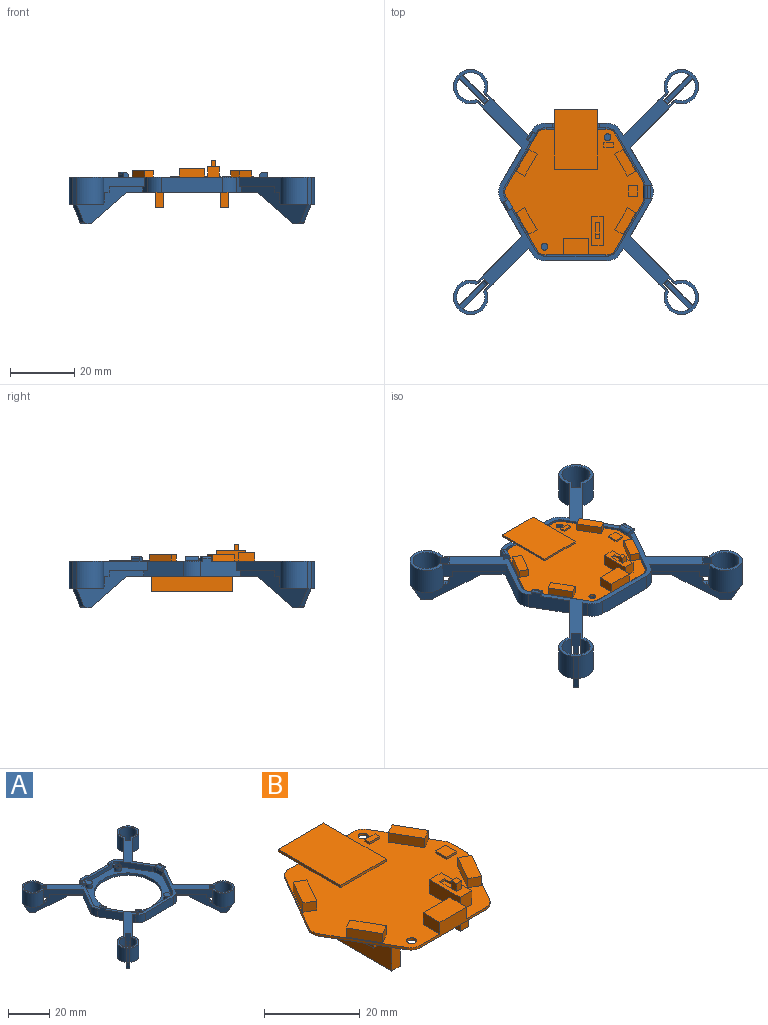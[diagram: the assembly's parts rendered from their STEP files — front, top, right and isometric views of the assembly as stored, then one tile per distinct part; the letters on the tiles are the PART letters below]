
ASSEMBLY  parts=2 mates=1
PART A: 187 faces, bbox 76.1x76.1x15.9 mm
  f0: plane 19.25x3.2mm, normal (0,1,0), area 60.2mm2, adj f2,f8,f69,f72,f78,f81,f117,f119
  f1: cylinder r=1.7mm len=3.4mm, axis (0,0,-1), area 22.2mm2, adj f72,f78,f118,f119
  f2: cylinder r=3.4mm len=3.2mm, axis (0,0,1), area 9.8mm2, adj f0,f8,f68,f72,f81,f116
  f3: plane 6.65x3.25mm, normal (0,0,1), area 10.1mm2, adj f4,f5,f62,f63,f71,f175,f184
  f4: plane 19.25x3.2mm, normal (0,-1,0), area 45.7mm2, adj f3,f7,f47,f63,f72,f75,f83,f113
  f5: plane 19.14x4.7mm, normal (0,1,0), area 75.5mm2, adj f3,f7,f23,f60,f71,f184,f185,f186
  f6: plane 41.4x23.95mm, normal (0,0,1), area 130.3mm2, adj f10,f11,f41,f45,f46,f49,f53,f61
  f7: plane 35.96x30.8mm, normal (0,0,1), area 137.2mm2, adj f4,f5,f13,f14,f39,f47,f58,f59
  f8: plane 76.11x35.96mm, normal (0,0,1), area 289.8mm2, adj f0,f2,f9,f15,f36,f37,f38,f41
  f9: cylinder r=5.35mm len=8.48mm, axis (0,0,1), area 119.1mm2, adj f8,f32,f52,f93,f100,f161
  f10: cylinder r=5.35mm len=8.48mm, axis (0,0,1), area 119.1mm2, adj f6,f28,f50,f88,f107,f160
  f11: cylinder r=5.35mm len=8.48mm, axis (0,0,1), area 119.1mm2, adj f6,f30,f33,f87,f106,f160
  f12: plane 4.18x0.46mm, normal (0,0,1), area 1.3mm2, adj f58,f162
  f13: cylinder r=5.35mm len=8.48mm, axis (0,0,1), area 119.1mm2, adj f7,f22,f85,f95,f110,f158
  f14: cylinder r=5.35mm len=8.48mm, axis (0,0,1), area 119.1mm2, adj f7,f24,f26,f84,f109,f158
  f15: cylinder r=5.35mm len=8.48mm, axis (0,0,1), area 119.1mm2, adj f8,f25,f90,f98,f103,f159
  f16: plane 20.55x20.55mm, normal (0.71,0.71,0), area 112.3mm2, adj f20,f23,f30,f33,f44,f45,f105,f120
  f17: plane 20.55x20.55mm, normal (0.71,-0.71,0), area 112.3mm2, adj f23,f25,f42,f54,f98,f102,f125,f145
  f18: plane 20.55x20.55mm, normal (-0.71,0.71,0), area 112.3mm2, adj f21,f22,f23,f39,f86,f95,f108,f126
  f19: plane 20.55x20.55mm, normal (-0.71,-0.71,0), area 112.3mm2, adj f23,f31,f34,f38,f73,f99,f131,f132
  f20: plane 5.38x3.4mm, normal (-0.61,0.61,-0.5), area 10.6mm2, adj f16,f121,f139,f160
  f21: plane 5.38x3.4mm, normal (0.61,0.61,-0.5), area 10.6mm2, adj f18,f128,f152,f158
  f22: plane 2.86x2.32mm, normal (0,0,-1), area 2.2mm2, adj f13,f18,f85,f108,f110,f126
  f23: plane 48.08x42.8mm, normal (0,0,-1), area 787.8mm2, adj f5,f16,f17,f18,f19,f37,f38,f39
  f24: plane 8.48x8.01mm, normal (0,0,-1), area 13mm2, adj f14,f94,f109,f128
  f25: plane 2.86x2.32mm, normal (0,0,-1), area 2.2mm2, adj f15,f17,f90,f102,f103,f125
  f26: plane 2.86x2.32mm, normal (0,0,-1), area 2.2mm2, adj f14,f84,f108,f109,f127,f128
  f27: plane 8.48x8.01mm, normal (0,0,-1), area 13mm2, adj f96,f97,f104,f124
  f28: plane 2.86x2.32mm, normal (0,0,-1), area 2.2mm2, adj f10,f88,f105,f107,f121,f122
  f29: plane 2.86x2.32mm, normal (0,0,-1), area 2.2mm2, adj f89,f96,f102,f104,f123,f124
  f30: plane 8.48x8.01mm, normal (0,0,-1), area 13mm2, adj f11,f16,f49,f106
  f31: plane 8.48x8.01mm, normal (0,0,-1), area 13mm2, adj f19,f36,f51,f101
  f32: plane 2.86x2.32mm, normal (0,0,-1), area 2.2mm2, adj f9,f93,f99,f100,f129,f130
  f33: plane 2.86x2.32mm, normal (0,0,-1), area 2.2mm2, adj f11,f16,f87,f105,f106,f120
  f34: plane 12.08x11.86mm, normal (0,0,-1), area 18.1mm2, adj f19,f38,f92,f131
  f35: plane 12.62x12.4mm, normal (0,0,-1), area 19mm2, adj f37,f93,f129,f130
  f36: cylinder r=5.35mm len=8.48mm, axis (0,0,1), area 119.1mm2, adj f8,f31,f73,f92,f101,f161
  f37: plane 12.47x7.2mm, normal (0.87,-0.5,0), area 64.2mm2, adj f8,f23,f35,f58,f93,f129
  f38: plane 4.7x2.41mm, normal (0.87,-0.5,0), area 9.6mm2, adj f8,f19,f23,f34,f57,f92
  f39: plane 4.7x2.41mm, normal (0.87,0.5,0), area 9.6mm2, adj f7,f18,f23,f60,f85,f86
  f40: plane 12.62x12.4mm, normal (0,0,-1), area 19mm2, adj f59,f84,f127,f128
  f41: plane 12.47x7.2mm, normal (-0.87,-0.5,0), area 67.2mm2, adj f6,f8,f23,f53,f89,f91,f124,f169
  f42: plane 12.08x11.86mm, normal (0,0,-1), area 18.1mm2, adj f17,f54,f90,f125
  f43: plane 12.62x12.4mm, normal (0,0,-1), area 19mm2, adj f46,f88,f121,f122
  f44: plane 12.08x11.86mm, normal (0,0,-1), area 18.1mm2, adj f16,f45,f87,f120
  f45: plane 5.7x2.6mm, normal (-0.87,0.5,0), area 12.6mm2, adj f6,f16,f23,f44,f71,f87,f173,f175
  f46: plane 12.47x7.2mm, normal (-0.87,0.5,0), area 64.2mm2, adj f6,f23,f43,f53,f88,f121
  f47: cylinder r=3.4mm len=3.2mm, axis (0,0,1), area 9.8mm2, adj f4,f7,f64,f72,f75,f112
  f48: cylinder r=1.7mm len=3.4mm, axis (0,0,-1), area 22.2mm2, adj f72,f75,f112,f113
  f49: cylinder r=4.35mm len=8.7mm, axis (0,0,1), area 205.6mm2, adj f6,f30,f50,f106,f107,f144
  f50: plane 8.48x8.01mm, normal (0,0,-1), area 13mm2, adj f10,f49,f107,f121
  f51: cylinder r=4.35mm len=8.7mm, axis (0,0,1), area 205.6mm2, adj f8,f31,f52,f100,f101,f132
  f52: plane 8.48x8.01mm, normal (0,0,-1), area 13mm2, adj f9,f51,f100,f129
  f53: cylinder r=5mm len=5mm, axis (0,0,1), area 24.6mm2, adj f6,f23,f41,f46
  f54: plane 4.7x2.41mm, normal (-0.87,-0.5,0), area 9.6mm2, adj f8,f17,f23,f42,f55,f90
  f55: cylinder r=5mm len=4.7mm, axis (0,0,1), area 24.6mm2, adj f8,f23,f54,f56
  f56: plane 19.14x4.7mm, normal (0,-1,0), area 90mm2, adj f8,f23,f55,f57
  f57: cylinder r=5mm len=4.7mm, axis (0,0,1), area 24.6mm2, adj f8,f23,f38,f56
  f58: cylinder r=5mm len=5mm, axis (0,0,1), area 24.6mm2, adj f7,f8,f12,f23,f37,f59
  f59: plane 12.47x7.2mm, normal (0.87,0.5,0), area 64.2mm2, adj f7,f23,f40,f58,f84,f128
  f60: cylinder r=5mm len=4.7mm, axis (0,0,1), area 24.6mm2, adj f5,f7,f23,f39
  f61: cylinder r=3.4mm len=3.4mm, axis (0,0,1), area 11.4mm2, adj f6,f62,f70,f72
  f62: plane 16.5x9.53mm, normal (0.87,-0.5,0), area 61mm2, adj f3,f6,f61,f63,f72,f177
  f63: cylinder r=3.4mm len=3.2mm, axis (0,0,1), area 9.8mm2, adj f3,f4,f62,f72,f83,f115
  f64: plane 14.41x8.32mm, normal (-0.87,-0.5,0), area 53.2mm2, adj f7,f47,f65,f72
  f65: cylinder r=3.4mm len=3.2mm, axis (0,0,1), area 5.7mm2, adj f7,f64,f66,f72
  f66: plane 4.18x3.2mm, normal (-1,0,0), area 13.4mm2, adj f65,f67,f72,f167
  f67: cylinder r=3.4mm len=3.2mm, axis (0,0,1), area 5.7mm2, adj f8,f66,f68,f72
  f68: plane 14.41x8.32mm, normal (-0.87,0.5,0), area 53.2mm2, adj f2,f8,f67,f72
  f69: cylinder r=3.4mm len=3.2mm, axis (0,0,1), area 9.8mm2, adj f0,f8,f70,f72,f78,f118
  f70: plane 16.5x9.53mm, normal (0.87,0.5,0), area 61mm2, adj f6,f8,f61,f69,f72,f172
  f71: cylinder r=5mm len=4.7mm, axis (0,0,1), area 24.6mm2, adj f3,f5,f23,f45
  f72: plane 43.9x39.8mm, normal (0,0,1), area 482.4mm2, adj f0,f1,f2,f4,f47,f48,f61,f62
  f73: plane 2.86x2.32mm, normal (0,0,-1), area 2.2mm2, adj f19,f36,f92,f99,f101,f131
  f74: cylinder r=1.05mm len=2.3mm, axis (0,0,-1), area 15.2mm2, adj f75,f76
  f75: plane 4.6x3.4mm, normal (0,0,1), area 6.8mm2, adj f4,f47,f48,f74,f112,f113
  f76: plane 2.1x2.1mm, normal (0,0,1), area 3.5mm2, adj f74
  f77: cylinder r=1.05mm len=2.3mm, axis (0,0,-1), area 15.2mm2, adj f78,f79
  f78: plane 4.6x3.4mm, normal (0,0,1), area 6.8mm2, adj f0,f1,f69,f77,f118,f119
  f79: plane 2.1x2.1mm, normal (0,0,1), area 3.5mm2, adj f77
  f80: cylinder r=1.7mm len=3.4mm, axis (0,0,-1), area 22.2mm2, adj f72,f81,f116,f117
  f81: plane 4.6x3.4mm, normal (0,0,1), area 10.3mm2, adj f0,f2,f80,f116,f117
  f82: cylinder r=1.7mm len=3.4mm, axis (0,0,-1), area 22.2mm2, adj f72,f83,f114,f115
  f83: plane 4.6x3.4mm, normal (0,0,1), area 10.3mm2, adj f4,f63,f82,f114,f115
  f84: plane 13.84x13.84mm, normal (0.71,-0.71,0), area 62mm2, adj f7,f14,f26,f40,f59,f127
  f85: plane 13.09x13.09mm, normal (-0.71,0.71,0), area 58.9mm2, adj f7,f13,f22,f39,f86,f126
  f86: plane 12.08x11.86mm, normal (0,0,-1), area 18.1mm2, adj f18,f39,f85,f126
  f87: plane 13.09x13.09mm, normal (0.71,0.71,0), area 58.9mm2, adj f6,f11,f33,f44,f45,f120
  f88: plane 13.84x13.84mm, normal (-0.71,-0.71,0), area 62mm2, adj f6,f10,f28,f43,f46,f122
  f89: plane 13.84x13.84mm, normal (-0.71,0.71,0), area 62mm2, adj f8,f29,f41,f91,f96,f123
  f90: plane 13.09x13.09mm, normal (0.71,-0.71,0), area 58.9mm2, adj f8,f15,f25,f42,f54,f125
  f91: plane 12.62x12.4mm, normal (0,0,-1), area 19mm2, adj f41,f89,f123,f124
  f92: plane 13.09x13.09mm, normal (-0.71,-0.71,0), area 58.9mm2, adj f8,f34,f36,f38,f73,f131
  f93: plane 13.84x13.84mm, normal (0.71,0.71,0), area 62mm2, adj f8,f9,f32,f35,f37,f130
  f94: cylinder r=4.35mm len=8.7mm, axis (0,0,1), area 205.6mm2, adj f7,f24,f95,f109,f110,f157
  f95: plane 8.48x8.01mm, normal (0,0,-1), area 13mm2, adj f13,f18,f94,f110
  f96: cylinder r=5.35mm len=8.48mm, axis (0,0,1), area 119.1mm2, adj f8,f27,f29,f89,f104,f159
  f97: cylinder r=4.35mm len=8.7mm, axis (0,0,1), area 205.6mm2, adj f8,f27,f98,f103,f104,f145
  f98: plane 8.48x8.01mm, normal (0,0,-1), area 13mm2, adj f15,f17,f97,f103
  f99: plane 7.4x1.98mm, normal (0.71,-0.71,0), area 17.8mm2, adj f8,f19,f32,f73,f100,f101,f129,f134
  f100: plane 8.4x1.93mm, normal (-0.71,-0.71,0), area 16.7mm2, adj f8,f9,f32,f51,f52,f99
  f101: plane 8.4x1.93mm, normal (0.71,0.71,0), area 16.7mm2, adj f8,f31,f36,f51,f73,f99
  f102: plane 7.4x1.98mm, normal (-0.71,-0.71,0), area 17.8mm2, adj f8,f17,f25,f29,f103,f104,f124,f146
  f103: plane 8.4x1.93mm, normal (-0.71,0.71,0), area 16.7mm2, adj f8,f15,f25,f97,f98,f102
  f104: plane 8.4x1.93mm, normal (0.71,-0.71,0), area 16.7mm2, adj f8,f27,f29,f96,f97,f102
  f105: plane 7.4x1.98mm, normal (-0.71,0.71,0), area 17.8mm2, adj f6,f16,f28,f33,f106,f107,f121,f143
  f106: plane 8.4x1.93mm, normal (-0.71,-0.71,0), area 16.7mm2, adj f6,f11,f30,f33,f49,f105
  f107: plane 8.4x1.93mm, normal (0.71,0.71,0), area 16.7mm2, adj f6,f10,f28,f49,f50,f105
  f108: plane 7.4x1.98mm, normal (0.71,0.71,0), area 17.8mm2, adj f7,f18,f22,f26,f109,f110,f128,f156
  f109: plane 8.4x1.93mm, normal (-0.71,0.71,0), area 16.7mm2, adj f7,f14,f24,f26,f94,f108
  f110: plane 8.4x1.93mm, normal (0.71,-0.71,0), area 16.7mm2, adj f7,f13,f22,f94,f95,f108
  f111: cylinder r=16.43mm len=32.86mm, axis (0,0,1), area 154.8mm2, adj f23,f72
  f112: plane 2.3x1.21mm, normal (1,0,0), area 2.8mm2, adj f47,f48,f72,f75
  f113: plane 2.3x1.28mm, normal (-1,0,0), area 2.9mm2, adj f4,f48,f72,f75
  f114: plane 2.3x1.28mm, normal (1,0,0), area 2.9mm2, adj f4,f72,f82,f83
  f115: plane 2.3x1.21mm, normal (-1,0,0), area 2.8mm2, adj f63,f72,f82,f83
  f116: plane 2.3x1.21mm, normal (1,0,0), area 2.8mm2, adj f2,f72,f80,f81
  f117: plane 2.3x1.28mm, normal (-1,0,0), area 2.9mm2, adj f0,f72,f80,f81
  f118: plane 2.3x1.21mm, normal (-1,0,0), area 2.8mm2, adj f1,f69,f72,f78
  f119: plane 2.3x1.28mm, normal (1,0,0), area 2.9mm2, adj f0,f1,f72,f78
  f120: plane 1.8x0.81mm, normal (0.71,-0.71,0), area 2.1mm2, adj f16,f33,f44,f87
  f121: plane 20.87x20.87mm, normal (-0.71,-0.71,0), area 113.1mm2, adj f20,f23,f28,f43,f46,f50,f105,f122
  f122: plane 1.8x0.81mm, normal (0.71,-0.71,0), area 2.1mm2, adj f28,f43,f88,f121
  f123: plane 1.8x0.81mm, normal (0.71,0.71,0), area 2.1mm2, adj f29,f89,f91,f124
  f124: plane 20.87x20.87mm, normal (-0.71,0.71,0), area 113.1mm2, adj f23,f27,f29,f41,f91,f102,f123,f145
  f125: plane 1.8x0.81mm, normal (0.71,0.71,0), area 2.1mm2, adj f17,f25,f42,f90
  f126: plane 1.8x0.81mm, normal (-0.71,-0.71,0), area 2.1mm2, adj f18,f22,f85,f86
  f127: plane 1.8x0.81mm, normal (-0.71,-0.71,0), area 2.1mm2, adj f26,f40,f84,f128
  f128: plane 20.87x20.87mm, normal (0.71,-0.71,0), area 113.1mm2, adj f21,f23,f24,f26,f40,f59,f108,f127
  f129: plane 20.87x20.87mm, normal (0.71,0.71,0), area 113.1mm2, adj f23,f32,f35,f37,f52,f99,f130,f132
  f130: plane 1.8x0.81mm, normal (-0.71,0.71,0), area 2.1mm2, adj f32,f35,f93,f129
  f131: plane 1.8x0.81mm, normal (-0.71,0.71,0), area 2.1mm2, adj f19,f34,f73,f92
  f132: plane 8.36x8.36mm, normal (0,0,1), area 17.3mm2, adj f19,f51,f129,f134
  f133: plane 5.38x3.4mm, normal (0.61,-0.61,-0.5), area 10.6mm2, adj f19,f129,f138,f161
  f134: cylinder r=1mm len=1.91mm, axis (0.71,0.71,0), area 2.7mm2, adj f19,f99,f129,f132
  f135: plane 12.16x12.16mm, normal (-0.37,0.37,-0.85), area 30.9mm2, adj f19,f23,f129,f136
  f136: cylinder r=1mm len=1.57mm, axis (0.71,0.71,0), area 0.9mm2, adj f19,f129,f135,f137
  f137: plane 2.71x2.71mm, normal (0,0,-1), area 3.6mm2, adj f19,f129,f136,f138
  f138: cylinder r=1mm len=1.81mm, axis (0.71,0.71,0), area 1.8mm2, adj f19,f129,f133,f137
  f139: cylinder r=1mm len=1.81mm, axis (0.71,0.71,0), area 1.8mm2, adj f16,f20,f121,f140
  f140: plane 2.71x2.71mm, normal (0,0,-1), area 3.6mm2, adj f16,f121,f139,f141
  f141: cylinder r=1mm len=1.57mm, axis (0.71,0.71,0), area 0.9mm2, adj f16,f121,f140,f142
  f142: plane 12.16x12.16mm, normal (0.37,-0.37,-0.85), area 30.9mm2, adj f16,f23,f121,f141
  f143: cylinder r=1mm len=1.91mm, axis (0.71,0.71,0), area 2.7mm2, adj f16,f105,f121,f144
  f144: plane 8.36x8.36mm, normal (0,0,1), area 17.3mm2, adj f16,f49,f121,f143
  f145: plane 8.36x8.36mm, normal (0,0,1), area 17.3mm2, adj f17,f97,f124,f146
  f146: cylinder r=1mm len=1.91mm, axis (0.71,-0.71,0), area 2.7mm2, adj f17,f102,f124,f145
  f147: plane 12.16x12.16mm, normal (0.37,0.37,-0.85), area 30.9mm2, adj f17,f23,f124,f148
  f148: cylinder r=1mm len=1.57mm, axis (0.71,-0.71,0), area 0.9mm2, adj f17,f124,f147,f149
  f149: plane 2.71x2.71mm, normal (0,0,-1), area 3.6mm2, adj f17,f124,f148,f150
  f150: cylinder r=1mm len=1.81mm, axis (0.71,-0.71,0), area 1.8mm2, adj f17,f124,f149,f151
  f151: plane 5.38x3.4mm, normal (-0.61,-0.61,-0.5), area 10.6mm2, adj f17,f124,f150,f159
  f152: cylinder r=1mm len=1.81mm, axis (0.71,-0.71,0), area 1.8mm2, adj f18,f21,f128,f153
  f153: plane 2.71x2.71mm, normal (0,0,-1), area 3.6mm2, adj f18,f128,f152,f154
  f154: cylinder r=1mm len=1.57mm, axis (0.71,-0.71,0), area 0.9mm2, adj f18,f128,f153,f155
  f155: plane 12.16x12.16mm, normal (-0.37,-0.37,-0.85), area 30.9mm2, adj f18,f23,f128,f154
  f156: cylinder r=1mm len=1.91mm, axis (0.71,-0.71,0), area 2.7mm2, adj f18,f108,f128,f157
  f157: plane 8.36x8.36mm, normal (0,0,1), area 17.3mm2, adj f18,f94,f128,f156
  f158: plane 8.52x1.2mm, normal (0.71,0.71,0), area 14.5mm2, adj f7,f13,f14,f18,f21,f128
  f159: plane 8.52x1.2mm, normal (-0.71,-0.71,0), area 14.5mm2, adj f8,f15,f17,f96,f124,f151
  f160: plane 8.52x1.2mm, normal (-0.71,0.71,0), area 14.5mm2, adj f6,f10,f11,f16,f20,f121
  f161: plane 8.52x1.2mm, normal (0.71,-0.71,0), area 14.5mm2, adj f8,f9,f19,f36,f129,f133
  f162: plane 4.18x1mm, normal (1,0,0), area 4.2mm2, adj f12,f163,f165,f180
  f163: plane 2.73x1.5mm, normal (0,1,0), area 3.7mm2, adj f7,f162,f164,f166,f167,f180,f183
  f164: plane 4.18x0.2mm, normal (-1,0,0), area 0.8mm2, adj f163,f165,f167,f183
  f165: plane 2.73x1.5mm, normal (0,-1,0), area 3.7mm2, adj f8,f162,f164,f166,f167,f180,f183
  f166: plane 4.18x0.93mm, normal (0,0,1), area 3.9mm2, adj f163,f165,f180,f183
  f167: plane 4.18x0.5mm, normal (0,0,-1), area 2.1mm2, adj f66,f163,f164,f165
  f168: plane 2.6x1.5mm, normal (0.87,0.5,0), area 0.6mm2, adj f169,f170,f172,f182
  f169: plane 1.73x1.5mm, normal (-0.5,0.87,0), area 2.6mm2, adj f6,f41,f168,f171,f172,f179,f182
  f170: plane 1.73x1.5mm, normal (0.5,-0.87,0), area 2.6mm2, adj f8,f41,f168,f171,f172,f179,f182
  f171: plane 2.7x1.67mm, normal (0,0,1), area 0.6mm2, adj f169,f170,f179,f182
  f172: plane 2.85x1.93mm, normal (0,0,-1), area 1.5mm2, adj f70,f168,f169,f170
  f173: plane 1.73x1.5mm, normal (-0.5,-0.87,0), area 2.6mm2, adj f6,f45,f174,f176,f177,f178,f181
  f174: plane 2.6x1.5mm, normal (0.87,-0.5,0), area 0.6mm2, adj f173,f175,f177,f181
  f175: plane 1.73x1.5mm, normal (0.5,0.87,0), area 2.6mm2, adj f3,f45,f174,f176,f177,f178,f181
  f176: plane 2.7x1.67mm, normal (0,0,1), area 0.6mm2, adj f173,f175,f178,f181
  f177: plane 2.85x1.93mm, normal (0,0,-1), area 1.5mm2, adj f62,f173,f174,f175
  f178: cylinder r=0.5mm len=2.85mm, axis (0.5,0.87,0), area 2.4mm2, adj f45,f173,f175,f176
  f179: cylinder r=0.5mm len=2.85mm, axis (0.5,-0.87,0), area 2.4mm2, adj f41,f169,f170,f171
  f180: cylinder r=0.5mm len=4.18mm, axis (0,-1,0), area 3.3mm2, adj f162,f163,f165,f166
  f181: cylinder r=1.3mm len=3.25mm, axis (-0.5,-0.87,0), area 6.1mm2, adj f173,f174,f175,f176
  f182: cylinder r=1.3mm len=3.25mm, axis (0.5,-0.87,0), area 6.1mm2, adj f168,f169,f170,f171
  f183: cylinder r=1.3mm len=4.18mm, axis (0,1,0), area 8.5mm2, adj f163,f164,f165,f166
  f184: plane 1.5x1mm, normal (1,0,0), area 1.5mm2, adj f3,f4,f5,f186
  f185: plane 1.5x1mm, normal (-1,0,0), area 1.5mm2, adj f4,f5,f7,f186
  f186: plane 14.5x1.5mm, normal (0,0,1), area 21.7mm2, adj f4,f5,f184,f185
PART B: 93 faces, bbox 43.1x45.1x14.6 mm
  f0: plane 3.5x1.5mm, normal (0,0,1), area 5.3mm2, adj f85,f86,f87,f91
  f1: plane 43.1x39mm, normal (0,0,1), area 963.3mm2, adj f7,f8,f9,f10,f11,f12,f13,f14
  f2: plane 25.4x8.5mm, normal (-1,0,0), area 178.5mm2, adj f6,f23,f24,f25,f36,f38,f39
  f3: plane 25.4x8.5mm, normal (1,0,0), area 178.5mm2, adj f6,f23,f24,f25,f29,f30,f31
  f4: plane 25.4x8.5mm, normal (1,0,0), area 178.5mm2, adj f6,f26,f27,f28,f32,f33,f34
  f5: plane 25.4x8.5mm, normal (-1,0,0), area 178.5mm2, adj f6,f26,f27,f28,f29,f30,f31
  f6: plane 43.1x39mm, normal (0,0,-1), area 633.5mm2, adj f2,f3,f4,f5,f7,f8,f9,f10
  f7: cylinder r=3mm len=3mm, axis (0,0,-1), area 1.9mm2, adj f1,f6,f8,f22
  f8: plane 16.5x9.53mm, normal (-0.87,-0.5,0), area 11.4mm2, adj f1,f6,f7,f9
  f9: cylinder r=3mm len=2.6mm, axis (0,0,-1), area 1.9mm2, adj f1,f6,f8,f10
  f10: plane 19.25x3.6mm, normal (0,-1,0), area 35.3mm2, adj f1,f6,f9,f11,f66,f68,f69
  f11: cylinder r=3mm len=2.6mm, axis (0,0,-1), area 1.9mm2, adj f1,f6,f10,f12
  f12: plane 14.41x8.32mm, normal (0.87,-0.5,0), area 10mm2, adj f1,f6,f11,f13
  f13: cylinder r=3mm len=1.5mm, axis (0,0,-1), area 0.9mm2, adj f1,f6,f12,f14
  f14: plane 4.18x0.6mm, normal (1,0,0), area 2.5mm2, adj f1,f6,f13,f15
  f15: cylinder r=3mm len=1.5mm, axis (0,0,-1), area 0.9mm2, adj f1,f6,f14,f16
  f16: plane 14.41x8.32mm, normal (0.87,0.5,0), area 10mm2, adj f1,f6,f15,f17
  f17: cylinder r=3mm len=2.6mm, axis (0,0,-1), area 1.9mm2, adj f1,f6,f16,f18
  f18: plane 19.25x0.6mm, normal (0,1,0), area 11.6mm2, adj f1,f6,f17,f19,f60
  f19: cylinder r=3mm len=2.6mm, axis (0,0,-1), area 1.9mm2, adj f1,f6,f18,f22
  f20: cylinder r=1.05mm len=2.1mm, axis (0,0,-1), area 4mm2, adj f1,f6
  f21: cylinder r=1.05mm len=2.1mm, axis (0,0,-1), area 4mm2, adj f1,f6
  f22: plane 16.5x9.53mm, normal (-0.87,0.5,0), area 11.4mm2, adj f1,f6,f7,f19
  f23: plane 8.5x2.54mm, normal (0,-1,0), area 21.6mm2, adj f2,f3,f6,f25
  f24: plane 8.5x2.54mm, normal (0,1,0), area 21.6mm2, adj f2,f3,f6,f25
  f25: plane 25.4x2.54mm, normal (0,0,-1), area 64.5mm2, adj f2,f3,f23,f24
  f26: plane 8.5x2.54mm, normal (0,1,0), area 21.6mm2, adj f4,f5,f6,f28
  f27: plane 8.5x2.54mm, normal (0,-1,0), area 21.6mm2, adj f4,f5,f6,f28
  f28: plane 25.4x2.54mm, normal (0,0,-1), area 64.5mm2, adj f4,f5,f26,f27
  f29: plane 22x17.78mm, normal (0,0,-1), area 391.2mm2, adj f3,f5,f30,f31
  f30: plane 17.78x1.7mm, normal (0,1,0), area 30.2mm2, adj f3,f5,f6,f29
  f31: plane 17.78x1.7mm, normal (0,-1,0), area 30.2mm2, adj f3,f5,f6,f29
  f32: plane 22x3.57mm, normal (0,0,-1), area 78.5mm2, adj f4,f33,f34,f35
  f33: plane 3.57x1.7mm, normal (0,1,0), area 6.1mm2, adj f4,f6,f32,f35
  f34: plane 3.57x1.7mm, normal (0,-1,0), area 6.1mm2, adj f4,f6,f32,f35
  f35: plane 22x1.7mm, normal (1,0,0), area 37.4mm2, adj f6,f32,f33,f34
  f36: plane 3.57x1.7mm, normal (0,-1,0), area 6.1mm2, adj f2,f6,f37,f39
  f37: plane 22x1.7mm, normal (-1,0,0), area 37.4mm2, adj f6,f36,f38,f39
  f38: plane 3.57x1.7mm, normal (0,1,0), area 6.1mm2, adj f2,f6,f37,f39
  f39: plane 22x3.57mm, normal (0,0,-1), area 78.5mm2, adj f2,f36,f37,f38
  f40: plane 6.82x3.94mm, normal (0.87,-0.5,0), area 18.5mm2, adj f1,f41,f43,f44
  f41: plane 2.6x2.35mm, normal (0.5,0.87,0), area 7mm2, adj f1,f40,f42,f44
  f42: plane 6.82x3.94mm, normal (-0.87,0.5,0), area 18.5mm2, adj f1,f41,f43,f44
  f43: plane 2.6x2.35mm, normal (-0.5,-0.87,0), area 7mm2, adj f1,f40,f42,f44
  f44: plane 8.32x6.53mm, normal (0,0,1), area 23.6mm2, adj f40,f41,f42,f43
  f45: plane 6.82x3.94mm, normal (0.87,0.5,0), area 18.5mm2, adj f1,f46,f48,f49
  f46: plane 2.6x2.35mm, normal (-0.5,0.87,0), area 7mm2, adj f1,f45,f47,f49
  f47: plane 6.82x3.94mm, normal (-0.87,-0.5,0), area 18.5mm2, adj f1,f46,f48,f49
  f48: plane 2.6x2.35mm, normal (0.5,-0.87,0), area 7mm2, adj f1,f45,f47,f49
  f49: plane 8.32x6.53mm, normal (0,0,1), area 23.6mm2, adj f45,f46,f47,f48
  f50: plane 2.6x2.35mm, normal (-0.5,-0.87,0), area 7mm2, adj f1,f51,f53,f54
  f51: plane 6.82x3.94mm, normal (0.87,-0.5,0), area 18.5mm2, adj f1,f50,f52,f54
  f52: plane 2.6x2.35mm, normal (0.5,0.87,0), area 7mm2, adj f1,f51,f53,f54
  f53: plane 6.82x3.94mm, normal (-0.87,0.5,0), area 18.5mm2, adj f1,f50,f52,f54
  f54: plane 8.32x6.53mm, normal (0,0,1), area 23.6mm2, adj f50,f51,f52,f53
  f55: plane 2.6x2.35mm, normal (0.5,-0.87,0), area 7mm2, adj f1,f56,f58,f59
  f56: plane 6.82x3.94mm, normal (0.87,0.5,0), area 18.5mm2, adj f1,f55,f57,f59
  f57: plane 2.6x2.35mm, normal (-0.5,0.87,0), area 7mm2, adj f1,f56,f58,f59
  f58: plane 6.82x3.94mm, normal (-0.87,-0.5,0), area 18.5mm2, adj f1,f55,f57,f59
  f59: plane 8.32x6.53mm, normal (0,0,1), area 23.6mm2, adj f55,f56,f57,f58
  f60: plane 13.5x6.09mm, normal (0,0,-1), area 82.2mm2, adj f18,f61,f62,f63
  f61: plane 18.5x0.6mm, normal (1,0,0), area 11.1mm2, adj f1,f60,f62,f64,f65
  f62: plane 13.5x0.6mm, normal (0,1,0), area 8.1mm2, adj f60,f61,f63,f65
  f63: plane 18.5x0.6mm, normal (-1,0,0), area 11.1mm2, adj f1,f60,f62,f64,f65
  f64: plane 13.5x0.6mm, normal (0,-1,0), area 8.1mm2, adj f1,f61,f63,f65
  f65: plane 18.5x13.5mm, normal (0,0,1), area 249.8mm2, adj f61,f62,f63,f64
  f66: plane 5x3mm, normal (1,0,0), area 15mm2, adj f1,f10,f67,f69
  f67: plane 7.9x3mm, normal (0,1,0), area 23.7mm2, adj f1,f66,f68,f69
  f68: plane 5x3mm, normal (-1,0,0), area 15mm2, adj f1,f10,f67,f69
  f69: plane 7.9x5mm, normal (0,0,1), area 39.5mm2, adj f10,f66,f67,f68
  f70: plane 1.4x0.5mm, normal (-1,0,0), area 0.7mm2, adj f1,f71,f73,f74
  f71: plane 3x0.5mm, normal (0,-1,0), area 1.5mm2, adj f1,f70,f72,f74
  f72: plane 1.4x0.5mm, normal (1,0,0), area 0.7mm2, adj f1,f71,f73,f74
  f73: plane 3x0.5mm, normal (0,1,0), area 1.5mm2, adj f1,f70,f72,f74
  f74: plane 3x1.4mm, normal (0,0,1), area 4.2mm2, adj f70,f71,f72,f73
  f75: plane 3.31x0.5mm, normal (-1,0,0), area 1.7mm2, adj f1,f76,f78,f79
  f76: plane 3x0.5mm, normal (0,-1,0), area 1.5mm2, adj f1,f75,f77,f79
  f77: plane 3.31x0.5mm, normal (1,0,0), area 1.7mm2, adj f1,f76,f78,f79
  f78: plane 3x0.5mm, normal (0,1,0), area 1.5mm2, adj f1,f75,f77,f79
  f79: plane 3.31x3mm, normal (0,0,1), area 9.9mm2, adj f75,f76,f77,f78
  f80: plane 9.1x3.54mm, normal (-1,0,0), area 32.2mm2, adj f1,f81,f83,f84
  f81: plane 3.54x3.5mm, normal (0,-1,0), area 12.4mm2, adj f1,f80,f82,f84
  f82: plane 9.1x3.54mm, normal (1,0,0), area 32.2mm2, adj f1,f81,f83,f84
  f83: plane 3.54x3.5mm, normal (0,1,0), area 12.4mm2, adj f1,f80,f82,f84
  f84: plane 9.1x3.5mm, normal (0,0,1), area 24.4mm2, adj f80,f81,f82,f83,f85,f86,f87,f88
  f85: plane 3.5x0.5mm, normal (1,0,0), area 1.7mm2, adj f0,f84,f87,f91
  f86: plane 3.5x0.5mm, normal (-1,0,0), area 1.7mm2, adj f0,f84,f87,f91
  f87: plane 1.5x0.5mm, normal (0,-1,0), area 0.7mm2, adj f0,f84,f85,f86
  f88: plane 2x1.5mm, normal (-1,0,0), area 3mm2, adj f84,f89,f91,f92
  f89: plane 2x1.5mm, normal (0,-1,0), area 3mm2, adj f84,f88,f90,f92
  f90: plane 2x1.5mm, normal (1,0,0), area 3mm2, adj f84,f89,f91,f92
  f91: plane 2.5x1.5mm, normal (0,1,0), area 3.8mm2, adj f0,f85,f86,f88,f90,f92
  f92: plane 1.5x1.5mm, normal (0,0,1), area 2.3mm2, adj f88,f89,f90,f91
PLACE A t=(-13.94,-10.75,2.21)mm
PLACE B t=(-13.94,-10.75,2.71)mm
MATE fastened B.f21 <-> A.f1  axis (0,0,-1) through (-23.75,-27.75,2.71)mm
